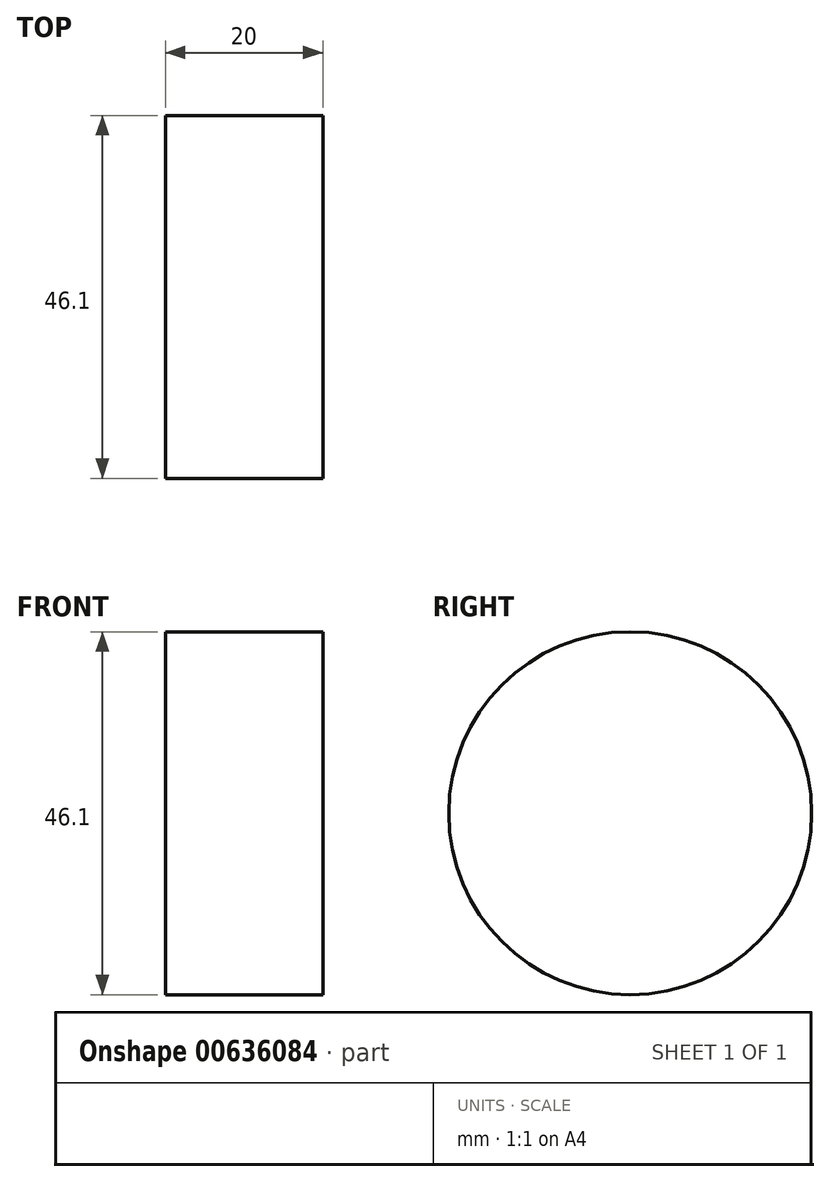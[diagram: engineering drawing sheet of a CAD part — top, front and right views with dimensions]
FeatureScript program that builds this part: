
annotation { "Feature Type Name" : "Feature", "Feature Type Description" : "" }
export const myFeature = defineFeature(function(context is Context, id is Id, definition is map)
    precondition{}
    {
        {
            var Q0;
            Q0=qCreatedBy(makeId("Right.planeOp"),FACE);
            var sketch = newSketch(context, id + "F0", { "sketchPlane" : qUnion([Q0])});
            skCircle(sketch, "E0", {"center": v(0, 0) * mm, "radius": 23.05 * mm});
            skSolve(sketch);
        }
        {
            var Q0;
            Q0=makeQuery(id+"F0.imprint","IMPRINT",FACE,{"disambiguationData":[TD([[makeQuery(id+"F0.imprint","IMPRINT",EDGE,{"derivedFrom":sQuery(id+"F0.wireOp",EDGE,"E0")}),1.0]])]});
            extrude(context, id + "F1", {"entities" : qUnion([Q0]), "depth" : 20 * mm, "offsetDistance" : 25 * mm});
        }
    });
